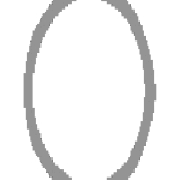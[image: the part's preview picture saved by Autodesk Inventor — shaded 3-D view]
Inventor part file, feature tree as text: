
AUTODESK INVENTOR PART (.ipt)
format: ipt  version: 2021 (Build 250183000, 183)  size: 112,128 bytes
history: native  units: in
note: dims shown in document units (in); Inventor stores cm internally (conversion verified against a paired STEP export)
features: other x4, sketch x3, plane x1
ambient origin geometry x8: Origin, YZ Plane, XZ Plane, XY Plane, X Axis, Y Axis, Z Axis, Center Point
bodies: Solid1 (feature_tree), Body (feature_tree)
feature tree (8):
  other  "Driven Length"
  other  "Frame Generator"
  other  "Start Plane"
  other  "End Plane"
  sketch  "Sketch"  dims[d2=13.5957in d4=-0.0in d5=13.5957in d6=0.12in d7=0.0in d8=90.0deg d9=13.5957in]
  sketch  "Sketch2"  dims[d0=1.0in]
  plane  "Work Plane3"
  sketch  "Sketch3"  dims[d1=0.065in]
